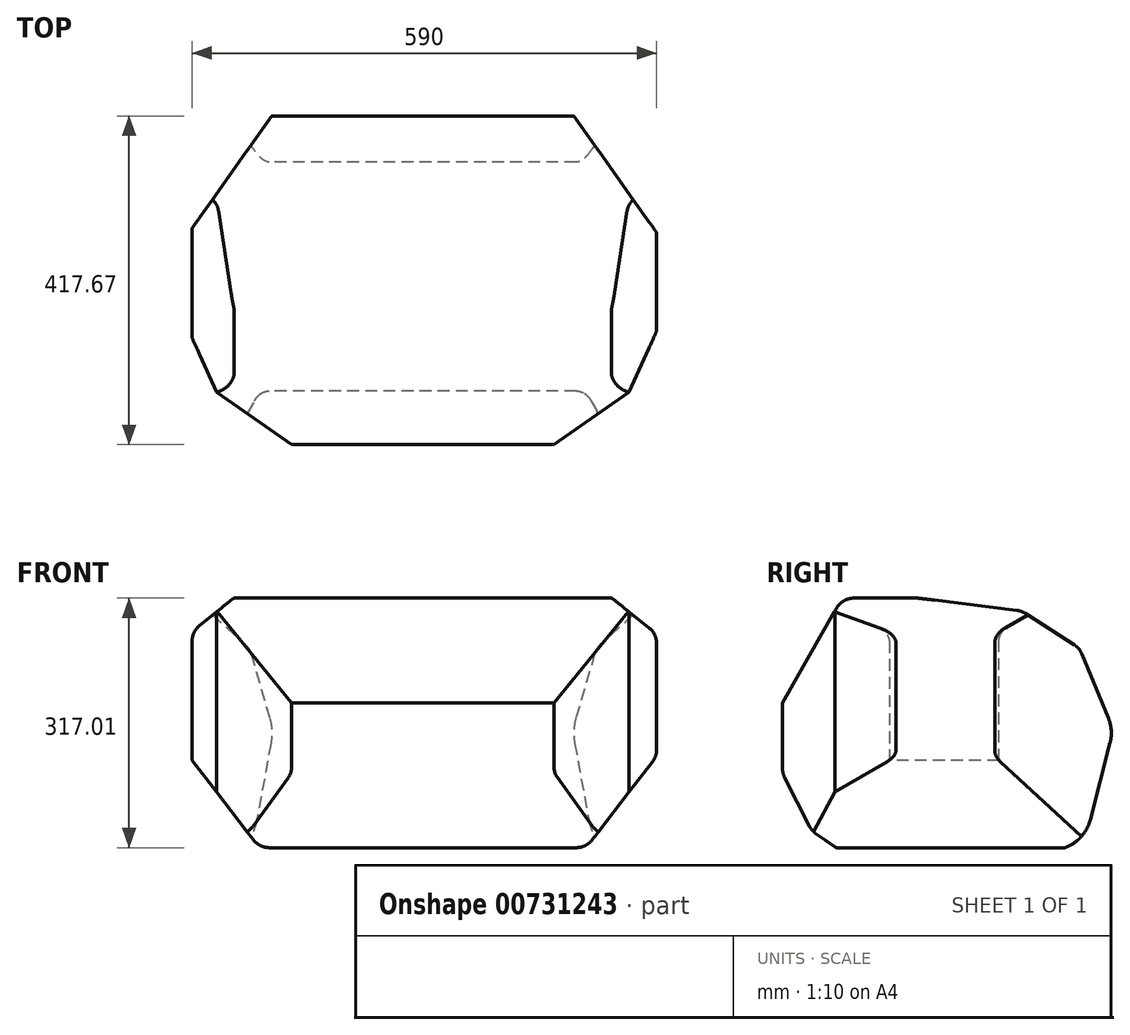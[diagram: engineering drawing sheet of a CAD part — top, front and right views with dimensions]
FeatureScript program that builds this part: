
annotation { "Feature Type Name" : "Feature", "Feature Type Description" : "" }
export const myFeature = defineFeature(function(context is Context, id is Id, definition is map)
    precondition{}
    {
        {
            var Q0;
            Q0=qCreatedBy(makeId("Front.planeOp"),FACE);
            var sketch = newSketch(context, id + "F0", { "sketchPlane" : qUnion([Q0])});
            skLineSegment(sketch, "E0", {"start": v(-293.04, 235.87) * mm, "end": v(296.96, 235.87) * mm, "construction": true});
            skLineSegment(sketch, "E1", {"start": v(0, 18.33) * mm, "end": v(0, 338.33) * mm, "construction": true});
            skLineSegment(sketch, "E2.bottom", {"start": v(-195, 18.33) * mm, "end": v(195, 18.33) * mm});
            skLineSegment(sketch, "E2.top", {"start": v(-227.65, 338.33) * mm, "end": v(227.65, 338.33) * mm});
            skLineSegment(sketch, "E2.left", {"start": v(-293.04, 18.33) * mm, "end": v(-293.04, 280.98) * mm});
            skLineSegment(sketch, "E2.right", {"start": v(296.96, 142.72) * mm, "end": v(296.96, 277.85) * mm});
            skLineSegment(sketch, "E3", {"start": v(215.08, 28.19) * mm, "end": v(291.65, 127.18) * mm});
            skLineSegment(sketch, "E4", {"start": v(287.41, 297.7) * mm, "end": v(243.5, 332.77) * mm});
            skLineSegment(sketch, "E5.MirrorCS", {"start": v(-283.5, 300.82) * mm, "end": v(-243.5, 332.77) * mm});
            skLineSegment(sketch, "E6.MirrorCS", {"start": v(-215.08, 28.19) * mm, "end": v(-293.04, 128.98) * mm});
            skPoint(sketch, "E7.orphan", {"position": v(-296.96, 290.07) * mm});
            skPoint(sketch, "E8.orphan", {"position": v(-296.96, 134.04) * mm});
            skPoint(sketch, "E9.newPointA", {"position": v(-207.46, 18.33) * mm});
            skPoint(sketch, "E9.newPointB", {"position": v(-293.04, 18.33) * mm});
            skArc(sketch, "E9.filletArc", {"start": v(-215.08, 28.19) * mm, "mid": v(-206.18, 20.92) * mm, "end": v(-195, 18.33) * mm});
            skPoint(sketch, "E10.newPointB", {"position": v(207.46, 18.33) * mm});
            skArc(sketch, "E10.filletArc", {"start": v(195, 18.33) * mm, "mid": v(206.18, 20.92) * mm, "end": v(215.08, 28.19) * mm});
            skPoint(sketch, "E11.newPointA", {"position": v(296.96, 134.04) * mm});
            skArc(sketch, "E11.filletArc", {"start": v(291.65, 127.18) * mm, "mid": v(295.6, 134.5) * mm, "end": v(296.96, 142.72) * mm});
            skPoint(sketch, "E12.newPointB", {"position": v(296.96, 290.07) * mm});
            skArc(sketch, "E12.filletArc", {"start": v(296.96, 277.85) * mm, "mid": v(294.45, 288.86) * mm, "end": v(287.41, 297.7) * mm});
            skPoint(sketch, "E13.newPointA", {"position": v(236.55, 338.33) * mm});
            skPoint(sketch, "E13.newPointB", {"position": v(296.96, 338.33) * mm});
            skArc(sketch, "E13.filletArc", {"start": v(243.5, 332.77) * mm, "mid": v(236.05, 336.9) * mm, "end": v(227.65, 338.33) * mm});
            skPoint(sketch, "E14.newPointB", {"position": v(-236.55, 338.33) * mm});
            skArc(sketch, "E14.filletArc", {"start": v(-227.65, 338.33) * mm, "mid": v(-236.05, 336.9) * mm, "end": v(-243.5, 332.77) * mm});
            skArc(sketch, "E15.filletArc", {"start": v(-283.5, 300.82) * mm, "mid": v(-290.53, 291.99) * mm, "end": v(-293.04, 280.98) * mm});
            skSolve(sketch);
        }
        {
            var Q0;
            Q0=qCreatedBy(makeId("Right.planeOp"),FACE);
            var sketch = newSketch(context, id + "F1", { "sketchPlane" : qUnion([Q0])});
            skLineSegment(sketch, "E16", {"start": v(122.6, 15.34) * mm, "end": v(122.6, 335.34) * mm, "construction": true});
            skLineSegment(sketch, "E17", {"start": v(122.6, 15.34) * mm, "end": v(341.6, 15.34) * mm});
            skLineSegment(sketch, "E18", {"start": v(390.78, 53.43) * mm, "end": v(416.05, 151.21) * mm});
            skLineSegment(sketch, "E19", {"start": v(413.82, 183.3) * mm, "end": v(380.43, 264.2) * mm});
            skLineSegment(sketch, "E20", {"start": v(370.69, 275.86) * mm, "end": v(308.22, 316.02) * mm});
            skLineSegment(sketch, "E21", {"start": v(297.6, 319.87) * mm, "end": v(173.55, 335.15) * mm});
            skLineSegment(sketch, "E22", {"start": v(170.44, 335.34) * mm, "end": v(122.6, 335.34) * mm});
            skLineSegment(sketch, "E23", {"start": v(68.61, 322.5) * mm, "end": v(0, 201.92) * mm});
            skLineSegment(sketch, "E24", {"start": v(0, 201.92) * mm, "end": v(0, 118.96) * mm});
            skLineSegment(sketch, "E25", {"start": v(2.75, 107.47) * mm, "end": v(34.22, 45.46) * mm});
            skLineSegment(sketch, "E26", {"start": v(42.42, 36.06) * mm, "end": v(65.87, 19.84) * mm});
            skLineSegment(sketch, "E27", {"start": v(80.32, 15.34) * mm, "end": v(122.6, 15.34) * mm});
            skLineSegment(sketch, "E28", {"start": v(90.69, 335.34) * mm, "end": v(122.6, 335.34) * mm});
            skPoint(sketch, "E29.visualSharp", {"position": v(75.92, 335.34) * mm});
            skArc(sketch, "E29.filletArc", {"start": v(90.69, 335.34) * mm, "mid": v(77.92, 331.9) * mm, "end": v(68.61, 322.5) * mm});
            skPoint(sketch, "E30.visualSharp", {"position": v(172, 335.34) * mm});
            skArc(sketch, "E30.filletArc", {"start": v(173.55, 335.15) * mm, "mid": v(172, 335.29) * mm, "end": v(170.44, 335.34) * mm});
            skPoint(sketch, "E31.visualSharp", {"position": v(303.35, 319.16) * mm});
            skArc(sketch, "E31.filletArc", {"start": v(308.22, 316.02) * mm, "mid": v(303.12, 318.54) * mm, "end": v(297.6, 319.87) * mm});
            skPoint(sketch, "E32.visualSharp", {"position": v(377.4, 271.55) * mm});
            skArc(sketch, "E32.filletArc", {"start": v(380.43, 264.2) * mm, "mid": v(376.46, 270.77) * mm, "end": v(370.69, 275.86) * mm});
            skPoint(sketch, "E33.visualSharp", {"position": v(0, 112.88) * mm});
            skArc(sketch, "E33.filletArc", {"start": v(0, 118.96) * mm, "mid": v(0.7, 113.05) * mm, "end": v(2.75, 107.47) * mm});
            skPoint(sketch, "E34.visualSharp", {"position": v(37.13, 39.72) * mm});
            skArc(sketch, "E34.filletArc", {"start": v(34.22, 45.46) * mm, "mid": v(37.73, 40.25) * mm, "end": v(42.42, 36.06) * mm});
            skPoint(sketch, "E35.visualSharp", {"position": v(72.4, 15.34) * mm});
            skArc(sketch, "E35.filletArc", {"start": v(65.87, 19.84) * mm, "mid": v(72.75, 16.49) * mm, "end": v(80.32, 15.34) * mm});
            skPoint(sketch, "E36.visualSharp", {"position": v(380.94, 15.34) * mm});
            skArc(sketch, "E36.filletArc", {"start": v(341.6, 15.34) * mm, "mid": v(372.7, 25.97) * mm, "end": v(390.78, 53.43) * mm});
            skPoint(sketch, "E37.visualSharp", {"position": v(420.3, 167.63) * mm});
            skArc(sketch, "E37.filletArc", {"start": v(416.05, 151.21) * mm, "mid": v(417.55, 167.44) * mm, "end": v(413.82, 183.3) * mm});
            skSolve(sketch);
        }
        {
            var Q0;
            Q0=makeQuery(id+"F0.imprint","IMPRINT",FACE,{"disambiguationData":[TD([[makeQuery(id+"F0.imprint","IMPRINT",EDGE,{"derivedFrom":sQuery(id+"F0.wireOp",EDGE,"E2.bottom")}),1.0]])]});
            extrude(context, id + "F2", {"entities" : qUnion([Q0]), "oppositeDirection" : true, "depth" : 431.8 * mm});
        }
        {
            var Q0;
            Q0=qSketchRegion(id+"F1",true);
            extrude(context, id + "F3", {"entities" : qUnion([Q0]), "operationType" : NewBodyOperationType.INTERSECT, "endBound" : BoundingType.SYMMETRIC, "depth" : 600 * mm});
        }
        {
            var Q0;
            Q0=qCreatedBy(makeId("Top.planeOp"),FACE);
            var sketch = newSketch(context, id + "F4", { "sketchPlane" : qUnion([Q0])});
            skLineSegment(sketch, "E38", {"start": v(0, 0) * mm, "end": v(166.86, 0) * mm});
            skLineSegment(sketch, "E39", {"start": v(166.86, 0) * mm, "end": v(262.06, 66.6) * mm});
            skLineSegment(sketch, "E40", {"start": v(262.06, 66.6) * mm, "end": v(297.65, 145.78) * mm});
            skLineSegment(sketch, "E41", {"start": v(297.65, 145.78) * mm, "end": v(297.65, 268.56) * mm});
            skLineSegment(sketch, "E42", {"start": v(297.65, 268.56) * mm, "end": v(190.89, 418.91) * mm});
            skLineSegment(sketch, "E43", {"start": v(190.89, 418.91) * mm, "end": v(0, 418.91) * mm});
            skLineSegment(sketch, "E44.MirrorCS", {"start": v(-190.89, 418.91) * mm, "end": v(0, 418.91) * mm});
            skLineSegment(sketch, "E45.MirrorCS", {"start": v(-297.65, 268.56) * mm, "end": v(-190.89, 418.91) * mm});
            skLineSegment(sketch, "E46.MirrorCS", {"start": v(-297.65, 145.78) * mm, "end": v(-297.65, 268.56) * mm});
            skLineSegment(sketch, "E47.MirrorCS", {"start": v(-262.06, 66.6) * mm, "end": v(-297.65, 145.78) * mm});
            skLineSegment(sketch, "E48.MirrorCS", {"start": v(-166.86, 0) * mm, "end": v(-262.06, 66.6) * mm});
            skLineSegment(sketch, "E49.MirrorCS", {"start": v(0, 0) * mm, "end": v(-166.86, 0) * mm});
            skSolve(sketch);
        }
        {
            var Q0;
            Q0=qSketchRegion(id+"F4",true);
            extrude(context, id + "F5", {"entities" : qUnion([Q0]), "operationType" : NewBodyOperationType.INTERSECT, "endBound" : BoundingType.THROUGH_ALL, "depth" : 304.8 * mm});
        }
    });
